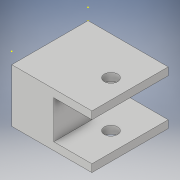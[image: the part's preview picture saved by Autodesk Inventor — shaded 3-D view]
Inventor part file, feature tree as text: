
AUTODESK INVENTOR PART (.ipt)
format: ipt  version: 2017 (Build 210142000, 142)  size: 144,384 bytes
history: native  units: in
note: dims shown in document units (in); Inventor stores cm internally (conversion verified against a paired STEP export)
features: sketch x10, extrude x6
ambient origin geometry x8: Origin, YZ Plane, XZ Plane, XY Plane, X Axis, Y Axis, Z Axis, Center Point
bodies: Solid1 (feature_tree)
feature tree (16):
  extrude  "Extrusion1"  Depth=0.8268in
  sketch  "Sketch2"  dims[d2=0.1969in d3=0.3937in]
  sketch  "Sketch3"  dims[d4=0.3937in d5=90.0deg]
  extrude  "Extrusion2"  Depth=0.3937in
  sketch  "Sketch5"  dims[d9=0.3937in d10=0.3937in]
  extrude  "Extrusion3"  TaperAngle=90.0deg  [1 undecoded]
  extrude  "Extrusion4"  Depth=0.7874in
  sketch  "Sketch8"  dims[d17=0.4331in]
  extrude  "Extrusion5"  Depth=0.3937in
  extrude  "Extrusion6"  Depth=0.4331in TaperAngle=0.0deg
  sketch  "Sketch1"  dims[d0=0.7874in d1=0.8268in]
  sketch  "Sketch4"  dims[d6=0.7874in d7=0.0in d8=0.2165in]
  sketch  "Sketch6"  dims[d11=0.4331in d12=0.0in d13=0.1181in d14=0.0in]
  sketch  "Sketch7"  dims[d15=0.1181in d16=0.0in]
  sketch  "Sketch9"  dims[d18=0.1378in]
  sketch  "Sketch10"  dims[d19=0.1969in d20=0.3937in d21=0.1378in d22=0.0in d23=0.1378in d24=0.1969in d25=0.3937in d26=0.1378in d27=0.0in]
note: 1 required parameter value undecoded (feature->parameter linkage not recoverable at this tier; creation-order binding heuristic only, values carry confidence <= 0.55)
